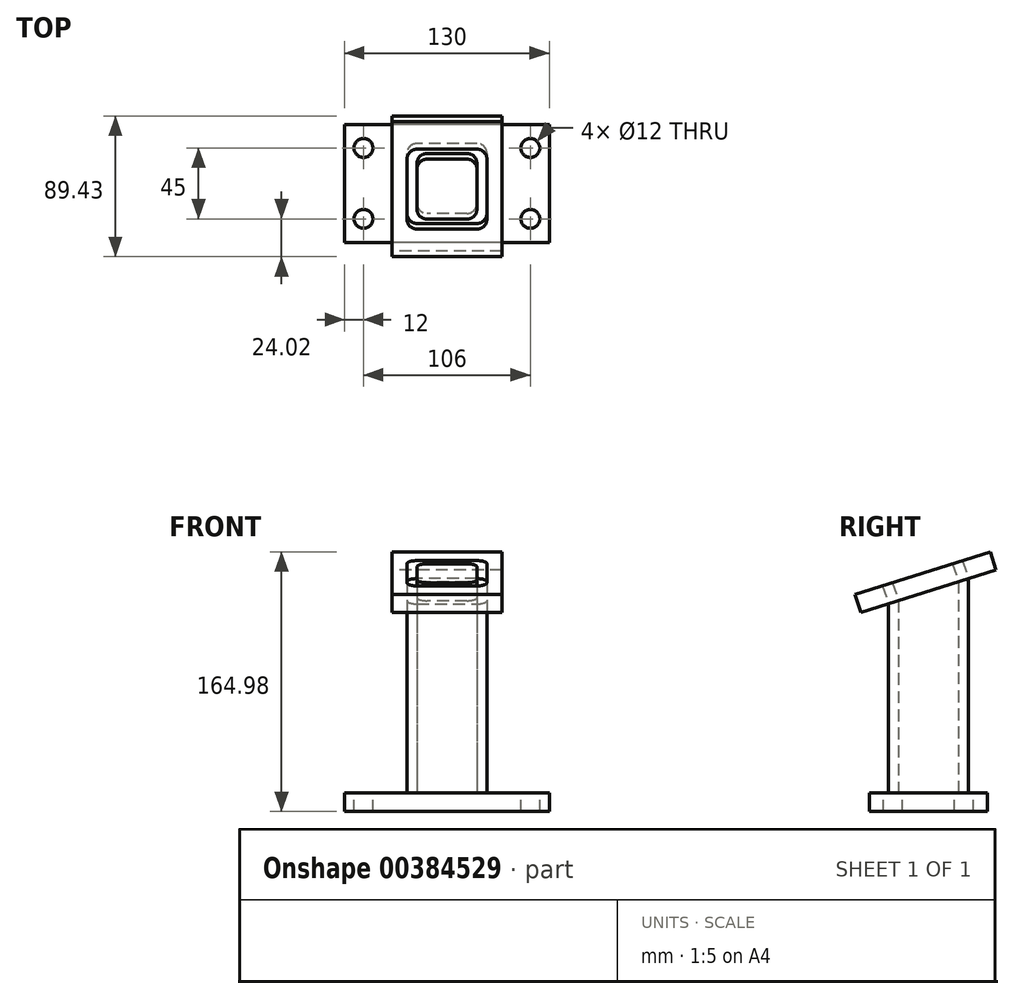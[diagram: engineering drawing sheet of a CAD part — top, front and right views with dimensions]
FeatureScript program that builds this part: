
annotation { "Feature Type Name" : "Feature", "Feature Type Description" : "" }
export const myFeature = defineFeature(function(context is Context, id is Id, definition is map)
    precondition{}
    {
        {
            var Q0;
            Q0=qCreatedBy(makeId("Top.planeOp"),FACE);
            var sketch = newSketch(context, id + "F0", { "sketchPlane" : qUnion([Q0])});
            skLineSegment(sketch, "E0.bottom", {"start": v(65, 37.5) * mm, "end": v(-65, 37.5) * mm});
            skLineSegment(sketch, "E0.top", {"start": v(65, -37.5) * mm, "end": v(-65, -37.5) * mm});
            skLineSegment(sketch, "E0.left", {"start": v(65, 37.5) * mm, "end": v(65, -37.5) * mm});
            skLineSegment(sketch, "E0.right", {"start": v(-65, 37.5) * mm, "end": v(-65, -37.5) * mm});
            skPoint(sketch, "E0.middle", {"position": v(0, 0) * mm});
            skSolve(sketch);
        }
        {
            var Q0;
            Q0=makeQuery(id+"F0.imprint","IMPRINT",FACE,{"disambiguationData":[TD([[makeQuery(id+"F0.imprint","IMPRINT",EDGE,{"derivedFrom":sQuery(id+"F0.wireOp",EDGE,"E0.bottom")}),1.0]])]});
            extrude(context, id + "F1", {"entities" : qUnion([Q0]), "depth" : -12 * mm});
        }
        {
            var Q0;
            Q0=makeQuery(id+"F1.opExtrude","CAP_FACE",FACE,{"disambiguationData":[OSD([sQuery(id+"F0.wireOp",EDGE,"E0.bottom"),sQuery(id+"F0.wireOp",EDGE,"E0.top"),sQuery(id+"F0.wireOp",EDGE,"E0.left"),sQuery(id+"F0.wireOp",EDGE,"E0.right")])],"isStart":true});
            var sketch = newSketch(context, id + "F2", { "sketchPlane" : qUnion([Q0])});
            skLineSegment(sketch, "E1.bottom", {"start": v(19.05, -25.4) * mm, "end": v(-19.05, -25.4) * mm});
            skLineSegment(sketch, "E1.top", {"start": v(19.05, 25.4) * mm, "end": v(-19.05, 25.4) * mm});
            skLineSegment(sketch, "E1.left", {"start": v(25.4, -19.05) * mm, "end": v(25.4, 19.05) * mm});
            skLineSegment(sketch, "E1.right", {"start": v(-25.4, -19.05) * mm, "end": v(-25.4, 19.05) * mm});
            skPoint(sketch, "E1.middle", {"position": v(0, 0) * mm});
            skPoint(sketch, "E2.visualSharp", {"position": v(-25.4, -25.4) * mm});
            skArc(sketch, "E2.filletArc", {"start": v(-25.4, -19.05) * mm, "mid": v(-23.54, -23.54) * mm, "end": v(-19.05, -25.4) * mm});
            skPoint(sketch, "E3.visualSharp", {"position": v(-25.4, 25.4) * mm});
            skArc(sketch, "E3.filletArc", {"start": v(-19.05, 25.4) * mm, "mid": v(-23.54, 23.54) * mm, "end": v(-25.4, 19.05) * mm});
            skPoint(sketch, "E4.visualSharp", {"position": v(25.4, 25.4) * mm});
            skArc(sketch, "E4.filletArc", {"start": v(25.4, 19.05) * mm, "mid": v(23.54, 23.54) * mm, "end": v(19.05, 25.4) * mm});
            skPoint(sketch, "E5.visualSharp", {"position": v(25.4, -25.4) * mm});
            skArc(sketch, "E5.filletArc", {"start": v(19.05, -25.4) * mm, "mid": v(23.54, -23.54) * mm, "end": v(25.4, -19.05) * mm});
            skLineSegment(sketch, "E6.bottom", {"start": v(12.7, 19.05) * mm, "end": v(-12.7, 19.05) * mm});
            skLineSegment(sketch, "E6.top", {"start": v(12.7, -19.05) * mm, "end": v(-12.7, -19.05) * mm});
            skLineSegment(sketch, "E6.left", {"start": v(19.05, 12.7) * mm, "end": v(19.05, -12.7) * mm});
            skLineSegment(sketch, "E6.right", {"start": v(-19.05, 12.7) * mm, "end": v(-19.05, -12.7) * mm});
            skArc(sketch, "E7.filletArc", {"start": v(-12.7, 19.05) * mm, "mid": v(-17.2, 17.2) * mm, "end": v(-19.05, 12.7) * mm});
            skArc(sketch, "E8.filletArc", {"start": v(19.05, 12.7) * mm, "mid": v(17.2, 17.2) * mm, "end": v(12.7, 19.05) * mm});
            skArc(sketch, "E9.filletArc", {"start": v(12.7, -19.05) * mm, "mid": v(17.2, -17.2) * mm, "end": v(19.05, -12.7) * mm});
            skArc(sketch, "E10.filletArc", {"start": v(-19.05, -12.7) * mm, "mid": v(-17.2, -17.2) * mm, "end": v(-12.7, -19.05) * mm});
            skSolve(sketch);
        }
        {
            var Q0;
            Q0=qSketchRegion(id+"F2",true);
            extrude(context, id + "F3", {"entities" : qUnion([Q0]), "operationType" : NewBodyOperationType.ADD, "depth" : 136 * mm});
        }
        {
            var Q0;
            {var subQ0=sQuery(id+"F0.wireOp",EDGE,"E0.left");var subQ1=sQuery(id+"F0.wireOp",EDGE,"E0.bottom");var subQ2=sQuery(id+"F0.wireOp",EDGE,"E0.right");var subQ3=sQuery(id+"F0.wireOp",EDGE,"E0.top");Q0=makeQuery(id+"F3.boolean.opBoolean","SPLIT",FACE,{"disambiguationData":[TD([makeQuery(id+"F1.opExtrude","SWEPT_FACE",FACE,{"disambiguationData":[OSD([subQ1])]})])],"derivedFrom":makeQuery(id+"F1.opExtrude","CAP_FACE",FACE,{"disambiguationData":[OSD([subQ1,subQ3,subQ0,subQ2])],"isStart":true})});}
            var sketch = newSketch(context, id + "F4", { "sketchPlane" : qUnion([Q0])});
            skLineSegment(sketch, "E11", {"start": v(-65, -37.5) * mm, "end": v(-53, -37.5) * mm, "construction": true});
            skLineSegment(sketch, "E12", {"start": v(-53, -37.5) * mm, "end": v(-53, -22.5) * mm, "construction": true});
            skLineSegment(sketch, "E13", {"start": v(-65, 37.5) * mm, "end": v(-53, 37.5) * mm, "construction": true});
            skLineSegment(sketch, "E14", {"start": v(-53, 37.5) * mm, "end": v(-53, 22.5) * mm, "construction": true});
            skLineSegment(sketch, "E15", {"start": v(65, 37.5) * mm, "end": v(53, 37.5) * mm, "construction": true});
            skLineSegment(sketch, "E16", {"start": v(65, -37.5) * mm, "end": v(53, -37.5) * mm, "construction": true});
            skLineSegment(sketch, "E17", {"start": v(53, -37.5) * mm, "end": v(53, -22.5) * mm, "construction": true});
            skLineSegment(sketch, "E18", {"start": v(53, 37.5) * mm, "end": v(53, 22.5) * mm, "construction": true});
            skSolve(sketch);
        }
        {
            var Q0;
            Q0=sQuery(id+"F4.wireOp",VERTEX,"E14.end");
            var Q1;
            Q1=sQuery(id+"F4.wireOp",VERTEX,"E18.end");
            var Q2;
            Q2=sQuery(id+"F4.wireOp",VERTEX,"E17.end");
            var Q3;
            Q3=sQuery(id+"F4.wireOp",VERTEX,"E12.end");
            var Q4;
            Q4=makeQuery(id+"F1.opExtrude","SWEPT_BODY",BODY,{"disambiguationData":[OSD([sQuery(id+"F0.wireOp",EDGE,"E0.bottom"),sQuery(id+"F0.wireOp",EDGE,"E0.top"),sQuery(id+"F0.wireOp",EDGE,"E0.left"),sQuery(id+"F0.wireOp",EDGE,"E0.right")])]});
            hole(context, id + "F5", {"style" : HoleStyle.SIMPLE, "endStyle" : HoleEndStyle.THROUGH, "holeDiameter" : 12 * mm, "isTappedThrough" : true, "tappedDepth" : 12 * mm, "tapClearance" : 3, "locations" : qUnion([Q0, Q1, Q2, Q3]), "scope" : qUnion([Q4])});
        }
        {
            var Q0;
            Q0=makeQuery(id+"F3.opExtrude","SWEPT_FACE",FACE,{"disambiguationData":[OSD([sQuery(id+"F2.wireOp",EDGE,"E1.left")])]});
            var sketch = newSketch(context, id + "F6", { "sketchPlane" : qUnion([Q0])});
            skLineSegment(sketch, "E19", {"start": v(-19.05, 136) * mm, "end": v(-25.4, 136) * mm, "construction": true});
            skLineSegment(sketch, "E20", {"start": v(-25.4, 136) * mm, "end": v(25.4, 136) * mm});
            skLineSegment(sketch, "E21", {"start": v(25.4, 136) * mm, "end": v(-25.4, 119.93) * mm});
            skLineSegment(sketch, "E22", {"start": v(-25.4, 136) * mm, "end": v(-25.4, 119.93) * mm});
            skSolve(sketch);
        }
        {
            var Q0;
            {var subQ3=sQuery(id+"F6.wireOp",EDGE,"E22");Q0=makeQuery(id+"F6.imprint","IMPRINT",FACE,{"disambiguationData":[TD([[makeQuery(id+"F6.imprint","IMPRINT",EDGE,{"derivedFrom":subQ3}),1.0]])]});}
            var Q1;
            {var subQ0=sQuery(id+"F6.wireOp",EDGE,"E20");var subQ1=sQuery(id+"F2.wireOp",EDGE,"E1.left");var subQ2=makeQuery(id+"F3.opExtrude","SWEPT_EDGE",EDGE,{"disambiguationData":[OSD([subQ1,sQuery(id+"F2.wireOp",EDGE,"E5.filletArc")])]});var subQ3=makeQuery(id+"F6.imprint","INTERSECT",VERTEX,{"derivedFrom":[subQ2,subQ0]});Q1=makeQuery(id+"F6.imprint","IMPRINT",FACE,{"disambiguationData":[TD([[makeQuery(id+"F6.imprint","IMPRINT",EDGE,{"disambiguationData":[TD([[subQ3,-1.0]])],"derivedFrom":subQ0}),-1.0]])]});}
            var Q2;
            {var subQ0=sQuery(id+"F6.wireOp",EDGE,"E20");var subQ3=sQuery(id+"F6.wireOp",EDGE,"E21");var subQ4=makeQuery(id+"F6.imprint","INTERSECT",VERTEX,{"derivedFrom":[subQ0,subQ3]});Q2=makeQuery(id+"F6.imprint","IMPRINT",FACE,{"disambiguationData":[TD([[makeQuery(id+"F6.imprint","IMPRINT",EDGE,{"disambiguationData":[TD([[subQ4,1.0]])],"derivedFrom":subQ0}),-1.0]])]});}
            extrude(context, id + "F7", {"entities" : qUnion([Q0, Q1, Q2]), "operationType" : NewBodyOperationType.REMOVE, "oppositeDirection" : true, "depth" : 50.8 * mm});
        }
        {
            var Q0;
            Q0=makeQuery(id+"F7.boolean.opBoolean","COPY",FACE,{"derivedFrom":makeQuery(id+"F7.opExtrude","SWEPT_FACE",FACE,{"disambiguationData":[OSD([sQuery(id+"F6.wireOp",EDGE,"E21")])]})});
            var sketch = newSketch(context, id + "F8", { "sketchPlane" : qUnion([Q0])});
            skLineSegment(sketch, "E23.bottom", {"start": v(35, -6.41) * mm, "end": v(-35, -6.41) * mm});
            skLineSegment(sketch, "E23.top", {"start": v(35, 83.59) * mm, "end": v(-35, 83.59) * mm});
            skLineSegment(sketch, "E23.left", {"start": v(35, -6.41) * mm, "end": v(35, 83.59) * mm});
            skLineSegment(sketch, "E23.right", {"start": v(-35, -6.41) * mm, "end": v(-35, 83.59) * mm});
            skPoint(sketch, "E23.middle", {"position": v(0, 38.59) * mm});
            skPoint(sketch, "E23.middle.positionSnap0", {"position": v(0, 58.57) * mm});
            skPoint(sketch, "E23.middle.positionSnap1", {"position": v(-19.05, 38.59) * mm});
            skPoint(sketch, "E23.centerSnap0", {"position": v(0, 58.57) * mm});
            skPoint(sketch, "E23.centerSnap1", {"position": v(-19.05, 38.59) * mm});
            skSolve(sketch);
        }
        {
            var Q0;
            {var subQ0=makeQuery(id+"F7.opExtrude","SWEPT_FACE",FACE,{"disambiguationData":[OSD([sQuery(id+"F6.wireOp",EDGE,"E21")])]});Q0=makeQuery(id+"F8.imprint","IMPRINT",FACE,{"disambiguationData":[TD([[makeQuery(id+"F8.imprint","IMPRINT",EDGE,{"derivedFrom":makeQuery(id+"F7.boolean.opBoolean","INTERSECT",EDGE,{"derivedFrom":[makeQuery(id+"F3.opExtrude","SWEPT_FACE",FACE,{"disambiguationData":[OSD([sQuery(id+"F2.wireOp",EDGE,"E6.bottom")])]}),subQ0]})}),1.0]])]});}
            var Q1;
            {var subQ0=sQuery(id+"F6.wireOp",EDGE,"E21");Q1=makeQuery(id+"F8.imprint","IMPRINT",FACE,{"disambiguationData":[TD([[makeQuery(id+"F8.imprint","IMPRINT",EDGE,{"derivedFrom":makeQuery(id+"F7.boolean.opBoolean","COPY",EDGE,{"derivedFrom":makeQuery(id+"F7.opExtrude","CAP_EDGE",EDGE,{"disambiguationData":[OSD([subQ0])],"isStart":true})})}),-1.0]])]});}
            var Q2;
            Q2=makeQuery(id+"F8.imprint","IMPRINT",FACE,{"disambiguationData":[TD([[makeQuery(id+"F8.imprint","IMPRINT",EDGE,{"derivedFrom":sQuery(id+"F8.wireOp",EDGE,"E23.bottom")}),-1.0]])]});
            extrude(context, id + "F9", {"entities" : qUnion([Q0, Q1, Q2]), "operationType" : NewBodyOperationType.ADD, "depth" : 12 * mm});
        }
    });
